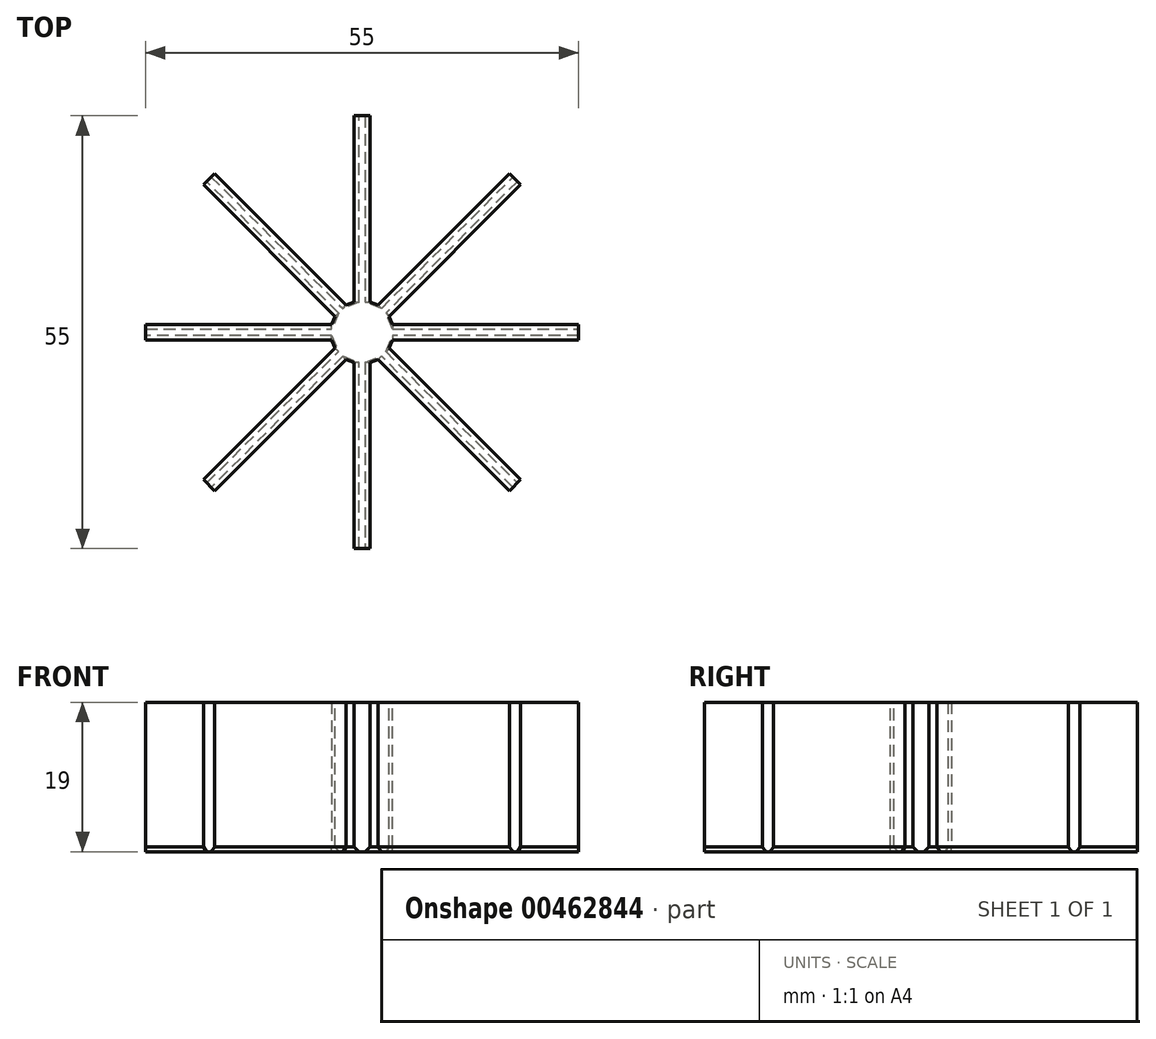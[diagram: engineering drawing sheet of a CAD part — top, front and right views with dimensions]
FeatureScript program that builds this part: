
annotation { "Feature Type Name" : "Feature", "Feature Type Description" : "" }
export const myFeature = defineFeature(function(context is Context, id is Id, definition is map)
    precondition{}
    {
        {
            var Q0;
            Q0=qCreatedBy(makeId("Top.planeOp"),FACE);
            var sketch = newSketch(context, id + "F0", { "sketchPlane" : qUnion([Q0])});
            skLineSegment(sketch, "E0.bottom", {"start": v(0, 0) * mm, "end": v(-2, 0) * mm});
            skLineSegment(sketch, "E0.top", {"start": v(0, 55) * mm, "end": v(-2, 55) * mm});
            skLineSegment(sketch, "E0.left", {"start": v(0, 0) * mm, "end": v(0, 55) * mm});
            skLineSegment(sketch, "E0.right", {"start": v(-2, 0) * mm, "end": v(-2, 55) * mm});
            skLineSegment(sketch, "E1", {"start": v(0, 0) * mm, "end": v(13.96, 0) * mm});
            skLineSegment(sketch, "E2", {"start": v(18.5, 0) * mm, "end": v(26.01, 0) * mm});
            skSolve(sketch);
        }
        {
            var Q0;
            Q0=makeQuery(id+"F0.imprint","IMPRINT",FACE,{"disambiguationData":[TD([[makeQuery(id+"F0.imprint","IMPRINT",EDGE,{"derivedFrom":sQuery(id+"F0.wireOp",EDGE,"E0.bottom")}),-1.0]])]});
            extrude(context, id + "F1", {"entities" : qUnion([Q0]), "depth" : 19 * mm});
        }
        {
            var Q0;
            Q0=qCreatedBy(makeId("Top.planeOp"),FACE);
            var sketch = newSketch(context, id + "F2", { "sketchPlane" : qUnion([Q0])});
            skLineSegment(sketch, "E3", {"start": v(13.67, 0) * mm, "end": v(36.23, 0) * mm});
            skSolve(sketch);
        }
        {
            var Q0;
            Q0=makeQuery(id+"F1.opExtrude","SWEPT_BODY",BODY,{"disambiguationData":[OSD([sQuery(id+"F0.wireOp",EDGE,"E0.bottom"),sQuery(id+"F0.wireOp",EDGE,"E0.top"),sQuery(id+"F0.wireOp",EDGE,"E0.left"),sQuery(id+"F0.wireOp",EDGE,"E0.right")])]});
            var Q1;
            Q1=sQuery(id+"F2.wireOp",EDGE,"E3");
            transform(context, id + "F3", {"entities" : qUnion([Q0]), "transformType" : TransformType.TRANSLATION_DISTANCE, "transformDirection" : qUnion([Q1]), "distance" : 1 * mm, "makeCopy" : false});
        }
        {
            var Q0;
            Q0=qCreatedBy(makeId("Top.planeOp"),FACE);
            var sketch = newSketch(context, id + "F4", { "sketchPlane" : qUnion([Q0])});
            skLineSegment(sketch, "E4", {"start": v(0, 62.06) * mm, "end": v(0, 72.35) * mm});
            skSolve(sketch);
        }
        {
            var Q0;
            Q0=makeQuery(id+"F1.opExtrude","SWEPT_BODY",BODY,{"disambiguationData":[OSD([sQuery(id+"F0.wireOp",EDGE,"E0.bottom"),sQuery(id+"F0.wireOp",EDGE,"E0.top"),sQuery(id+"F0.wireOp",EDGE,"E0.left"),sQuery(id+"F0.wireOp",EDGE,"E0.right")])]});
            var Q1;
            Q1=sQuery(id+"F4.wireOp",EDGE,"E4");
            transform(context, id + "F5", {"entities" : qUnion([Q0]), "transformType" : TransformType.TRANSLATION_DISTANCE, "transformDirection" : qUnion([Q1]), "distance" : 27.5 * mm, "oppositeDirection" : true, "makeCopy" : false});
        }
        {
            var Q0;
            Q0=qCreatedBy(makeId("Front.planeOp"),FACE);
            var sketch = newSketch(context, id + "F6", { "sketchPlane" : qUnion([Q0])});
            skLineSegment(sketch, "E5", {"start": v(0, 0) * mm, "end": v(0, 25.58) * mm});
            skSolve(sketch);
        }
        {
            var Q0;
            Q0=makeQuery(id+"F1.opExtrude","SWEPT_BODY",BODY,{"disambiguationData":[OSD([sQuery(id+"F0.wireOp",EDGE,"E0.bottom"),sQuery(id+"F0.wireOp",EDGE,"E0.top"),sQuery(id+"F0.wireOp",EDGE,"E0.left"),sQuery(id+"F0.wireOp",EDGE,"E0.right")])]});
            var Q1;
            Q1=sQuery(id+"F6.wireOp",EDGE,"E5");
            circularPattern(context, id + "F7", {"entities" : qUnion([Q0]), "axis" : qUnion([Q1]), "angle" : 360 * degree, "instanceCount" : 8, "equalSpace" : true});
        }
        {
            var Q0;
            Q0=makeQuery(id+"F1.opExtrude","SWEPT_BODY",BODY,{"disambiguationData":[OSD([sQuery(id+"F0.wireOp",EDGE,"E0.bottom"),sQuery(id+"F0.wireOp",EDGE,"E0.top"),sQuery(id+"F0.wireOp",EDGE,"E0.left"),sQuery(id+"F0.wireOp",EDGE,"E0.right")])]});
            var Q1;
            Q1=makeQuery(id+"F7.opPattern","COPY",BODY,{"derivedFrom":makeQuery(id+"F1.opExtrude","SWEPT_BODY",BODY,{"disambiguationData":[OSD([sQuery(id+"F0.wireOp",EDGE,"E0.bottom"),sQuery(id+"F0.wireOp",EDGE,"E0.top"),sQuery(id+"F0.wireOp",EDGE,"E0.left"),sQuery(id+"F0.wireOp",EDGE,"E0.right")])]}),"instanceName":"1"});
            var Q2;
            Q2=makeQuery(id+"F7.opPattern","COPY",BODY,{"derivedFrom":makeQuery(id+"F1.opExtrude","SWEPT_BODY",BODY,{"disambiguationData":[OSD([sQuery(id+"F0.wireOp",EDGE,"E0.bottom"),sQuery(id+"F0.wireOp",EDGE,"E0.top"),sQuery(id+"F0.wireOp",EDGE,"E0.left"),sQuery(id+"F0.wireOp",EDGE,"E0.right")])]}),"instanceName":"2"});
            var Q3;
            Q3=makeQuery(id+"F7.opPattern","COPY",BODY,{"derivedFrom":makeQuery(id+"F1.opExtrude","SWEPT_BODY",BODY,{"disambiguationData":[OSD([sQuery(id+"F0.wireOp",EDGE,"E0.bottom"),sQuery(id+"F0.wireOp",EDGE,"E0.top"),sQuery(id+"F0.wireOp",EDGE,"E0.left"),sQuery(id+"F0.wireOp",EDGE,"E0.right")])]}),"instanceName":"3"});
            var Q4;
            Q4=makeQuery(id+"F7.opPattern","COPY",BODY,{"derivedFrom":makeQuery(id+"F1.opExtrude","SWEPT_BODY",BODY,{"disambiguationData":[OSD([sQuery(id+"F0.wireOp",EDGE,"E0.bottom"),sQuery(id+"F0.wireOp",EDGE,"E0.top"),sQuery(id+"F0.wireOp",EDGE,"E0.left"),sQuery(id+"F0.wireOp",EDGE,"E0.right")])]}),"instanceName":"4"});
            var Q5;
            Q5=makeQuery(id+"F7.opPattern","COPY",BODY,{"derivedFrom":makeQuery(id+"F1.opExtrude","SWEPT_BODY",BODY,{"disambiguationData":[OSD([sQuery(id+"F0.wireOp",EDGE,"E0.bottom"),sQuery(id+"F0.wireOp",EDGE,"E0.top"),sQuery(id+"F0.wireOp",EDGE,"E0.left"),sQuery(id+"F0.wireOp",EDGE,"E0.right")])]}),"instanceName":"5"});
            var Q6;
            Q6=makeQuery(id+"F7.opPattern","COPY",BODY,{"derivedFrom":makeQuery(id+"F1.opExtrude","SWEPT_BODY",BODY,{"disambiguationData":[OSD([sQuery(id+"F0.wireOp",EDGE,"E0.bottom"),sQuery(id+"F0.wireOp",EDGE,"E0.top"),sQuery(id+"F0.wireOp",EDGE,"E0.left"),sQuery(id+"F0.wireOp",EDGE,"E0.right")])]}),"instanceName":"6"});
            var Q7;
            Q7=makeQuery(id+"F7.opPattern","COPY",BODY,{"derivedFrom":makeQuery(id+"F1.opExtrude","SWEPT_BODY",BODY,{"disambiguationData":[OSD([sQuery(id+"F0.wireOp",EDGE,"E0.bottom"),sQuery(id+"F0.wireOp",EDGE,"E0.top"),sQuery(id+"F0.wireOp",EDGE,"E0.left"),sQuery(id+"F0.wireOp",EDGE,"E0.right")])]}),"instanceName":"7"});
            booleanBodies(context, id + "F8", {"operationType" : BooleanOperationType.UNION, "tools" : qUnion([Q0, Q1, Q2, Q3, Q4, Q5, Q6, Q7])});
        }
        {
            var Q0;
            {var subQ0=sQuery(id+"F0.wireOp",EDGE,"E0.left");var subQ3=makeQuery(id+"F1.opExtrude","SWEPT_FACE",FACE,{"disambiguationData":[OSD([subQ0])]});Q0=makeQuery(id+"F8.opBoolean","SPLIT",EDGE,{"disambiguationData":[TD([subQ3])],"derivedFrom":makeQuery(id+"F7.opPattern","COPY",EDGE,{"derivedFrom":makeQuery(id+"F1.opExtrude","CAP_EDGE",EDGE,{"disambiguationData":[OSD([subQ0])],"isStart":true}),"instanceName":"3"})});}
            var Q1;
            {var subQ0=sQuery(id+"F0.wireOp",EDGE,"E0.left");var subQ1=sQuery(id+"F0.wireOp",EDGE,"E0.top");Q1=makeQuery(id+"F8.opBoolean","SPLIT",EDGE,{"disambiguationData":[TD([makeQuery(id+"F1.opExtrude","SWEPT_FACE",FACE,{"disambiguationData":[OSD([subQ1])]})])],"derivedFrom":makeQuery(id+"F1.opExtrude","CAP_EDGE",EDGE,{"disambiguationData":[OSD([subQ0])],"isStart":true})});}
            var Q2;
            {var subQ0=sQuery(id+"F0.wireOp",EDGE,"E0.right");var subQ2=sQuery(id+"F0.wireOp",EDGE,"E0.top");Q2=makeQuery(id+"F8.opBoolean","SPLIT",EDGE,{"disambiguationData":[TD([makeQuery(id+"F1.opExtrude","SWEPT_FACE",FACE,{"disambiguationData":[OSD([subQ2])]})])],"derivedFrom":makeQuery(id+"F1.opExtrude","CAP_EDGE",EDGE,{"disambiguationData":[OSD([subQ0])],"isStart":true})});}
            var Q3;
            {var subQ0=sQuery(id+"F0.wireOp",EDGE,"E0.right");var subQ1=sQuery(id+"F0.wireOp",EDGE,"E0.left");Q3=makeQuery(id+"F8.opBoolean","SPLIT",EDGE,{"disambiguationData":[TD([makeQuery(id+"F1.opExtrude","SWEPT_FACE",FACE,{"disambiguationData":[OSD([subQ0])]})])],"derivedFrom":makeQuery(id+"F7.opPattern","COPY",EDGE,{"derivedFrom":makeQuery(id+"F1.opExtrude","CAP_EDGE",EDGE,{"disambiguationData":[OSD([subQ1])],"isStart":true}),"instanceName":"1"})});}
            var Q4;
            {var subQ0=sQuery(id+"F0.wireOp",EDGE,"E0.right");var subQ2=sQuery(id+"F0.wireOp",EDGE,"E0.top");Q4=makeQuery(id+"F8.opBoolean","SPLIT",EDGE,{"disambiguationData":[TD([makeQuery(id+"F7.opPattern","COPY",FACE,{"derivedFrom":makeQuery(id+"F1.opExtrude","SWEPT_FACE",FACE,{"disambiguationData":[OSD([subQ2])]}),"instanceName":"1"})])],"derivedFrom":makeQuery(id+"F7.opPattern","COPY",EDGE,{"derivedFrom":makeQuery(id+"F1.opExtrude","CAP_EDGE",EDGE,{"disambiguationData":[OSD([subQ0])],"isStart":true}),"instanceName":"1"})});}
            var Q5;
            {var subQ0=sQuery(id+"F0.wireOp",EDGE,"E0.right");var subQ2=sQuery(id+"F0.wireOp",EDGE,"E0.top");Q5=makeQuery(id+"F8.opBoolean","SPLIT",EDGE,{"disambiguationData":[TD([makeQuery(id+"F7.opPattern","COPY",FACE,{"derivedFrom":makeQuery(id+"F1.opExtrude","SWEPT_FACE",FACE,{"disambiguationData":[OSD([subQ2])]}),"instanceName":"2"})])],"derivedFrom":makeQuery(id+"F7.opPattern","COPY",EDGE,{"derivedFrom":makeQuery(id+"F1.opExtrude","CAP_EDGE",EDGE,{"disambiguationData":[OSD([subQ0])],"isStart":true}),"instanceName":"2"})});}
            var Q6;
            {var subQ0=sQuery(id+"F0.wireOp",EDGE,"E0.right");var subQ1=sQuery(id+"F0.wireOp",EDGE,"E0.left");Q6=makeQuery(id+"F8.opBoolean","SPLIT",EDGE,{"disambiguationData":[TD([makeQuery(id+"F7.opPattern","COPY",FACE,{"derivedFrom":makeQuery(id+"F1.opExtrude","SWEPT_FACE",FACE,{"disambiguationData":[OSD([subQ0])]}),"instanceName":"2"})])],"derivedFrom":makeQuery(id+"F7.opPattern","COPY",EDGE,{"derivedFrom":makeQuery(id+"F1.opExtrude","CAP_EDGE",EDGE,{"disambiguationData":[OSD([subQ1])],"isStart":true}),"instanceName":"3"})});}
            var Q7;
            {var subQ0=sQuery(id+"F0.wireOp",EDGE,"E0.right");var subQ3=makeQuery(id+"F1.opExtrude","SWEPT_FACE",FACE,{"disambiguationData":[OSD([subQ0])]});Q7=makeQuery(id+"F8.opBoolean","SPLIT",EDGE,{"disambiguationData":[TD([subQ3])],"derivedFrom":makeQuery(id+"F7.opPattern","COPY",EDGE,{"derivedFrom":makeQuery(id+"F1.opExtrude","CAP_EDGE",EDGE,{"disambiguationData":[OSD([subQ0])],"isStart":true}),"instanceName":"3"})});}
            var Q8;
            {var subQ1=sQuery(id+"F0.wireOp",EDGE,"E0.left");var subQ2=sQuery(id+"F0.wireOp",EDGE,"E0.bottom");Q8=makeQuery(id+"F8.opBoolean","SPLIT",EDGE,{"disambiguationData":[TD([makeQuery(id+"F1.opExtrude","SWEPT_FACE",FACE,{"disambiguationData":[OSD([subQ2])]})])],"derivedFrom":makeQuery(id+"F1.opExtrude","CAP_EDGE",EDGE,{"disambiguationData":[OSD([subQ1])],"isStart":true})});}
            var Q9;
            {var subQ0=sQuery(id+"F0.wireOp",EDGE,"E0.right");var subQ1=sQuery(id+"F0.wireOp",EDGE,"E0.left");Q9=makeQuery(id+"F8.opBoolean","SPLIT",EDGE,{"disambiguationData":[TD([makeQuery(id+"F1.opExtrude","SWEPT_FACE",FACE,{"disambiguationData":[OSD([subQ1])]})])],"derivedFrom":makeQuery(id+"F7.opPattern","COPY",EDGE,{"derivedFrom":makeQuery(id+"F1.opExtrude","CAP_EDGE",EDGE,{"disambiguationData":[OSD([subQ0])],"isStart":true}),"instanceName":"1"})});}
            var Q10;
            {var subQ1=sQuery(id+"F0.wireOp",EDGE,"E0.left");var subQ2=sQuery(id+"F0.wireOp",EDGE,"E0.bottom");Q10=makeQuery(id+"F8.opBoolean","SPLIT",EDGE,{"disambiguationData":[TD([makeQuery(id+"F7.opPattern","COPY",FACE,{"derivedFrom":makeQuery(id+"F1.opExtrude","SWEPT_FACE",FACE,{"disambiguationData":[OSD([subQ2])]}),"instanceName":"1"})])],"derivedFrom":makeQuery(id+"F7.opPattern","COPY",EDGE,{"derivedFrom":makeQuery(id+"F1.opExtrude","CAP_EDGE",EDGE,{"disambiguationData":[OSD([subQ1])],"isStart":true}),"instanceName":"1"})});}
            var Q11;
            {var subQ0=sQuery(id+"F0.wireOp",EDGE,"E0.right");var subQ1=sQuery(id+"F0.wireOp",EDGE,"E0.left");Q11=makeQuery(id+"F8.opBoolean","SPLIT",EDGE,{"disambiguationData":[TD([makeQuery(id+"F7.opPattern","COPY",FACE,{"derivedFrom":makeQuery(id+"F1.opExtrude","SWEPT_FACE",FACE,{"disambiguationData":[OSD([subQ1])]}),"instanceName":"1"})])],"derivedFrom":makeQuery(id+"F7.opPattern","COPY",EDGE,{"derivedFrom":makeQuery(id+"F1.opExtrude","CAP_EDGE",EDGE,{"disambiguationData":[OSD([subQ0])],"isStart":true}),"instanceName":"2"})});}
            var Q12;
            {var subQ1=sQuery(id+"F0.wireOp",EDGE,"E0.left");var subQ2=sQuery(id+"F0.wireOp",EDGE,"E0.bottom");Q12=makeQuery(id+"F8.opBoolean","SPLIT",EDGE,{"disambiguationData":[TD([makeQuery(id+"F7.opPattern","COPY",FACE,{"derivedFrom":makeQuery(id+"F1.opExtrude","SWEPT_FACE",FACE,{"disambiguationData":[OSD([subQ2])]}),"instanceName":"2"})])],"derivedFrom":makeQuery(id+"F7.opPattern","COPY",EDGE,{"derivedFrom":makeQuery(id+"F1.opExtrude","CAP_EDGE",EDGE,{"disambiguationData":[OSD([subQ1])],"isStart":true}),"instanceName":"2"})});}
            var Q13;
            {var subQ0=sQuery(id+"F0.wireOp",EDGE,"E0.right");var subQ1=sQuery(id+"F0.wireOp",EDGE,"E0.left");Q13=makeQuery(id+"F8.opBoolean","SPLIT",EDGE,{"disambiguationData":[TD([makeQuery(id+"F7.opPattern","COPY",FACE,{"derivedFrom":makeQuery(id+"F1.opExtrude","SWEPT_FACE",FACE,{"disambiguationData":[OSD([subQ1])]}),"instanceName":"2"})])],"derivedFrom":makeQuery(id+"F7.opPattern","COPY",EDGE,{"derivedFrom":makeQuery(id+"F1.opExtrude","CAP_EDGE",EDGE,{"disambiguationData":[OSD([subQ0])],"isStart":true}),"instanceName":"3"})});}
            var Q14;
            {var subQ0=makeQuery(id+"F1.opExtrude","SWEPT_FACE",FACE,{"disambiguationData":[OSD([sQuery(id+"F0.wireOp",EDGE,"E0.right")])]});var subQ1=makeQuery(id+"F1.opExtrude","SWEPT_FACE",FACE,{"disambiguationData":[OSD([sQuery(id+"F0.wireOp",EDGE,"E0.left")])]});Q14=makeQuery(id+"F8.opBoolean","INTERSECT",EDGE,{"derivedFrom":[subQ1,makeQuery(id+"F7.opPattern","COPY",FACE,{"derivedFrom":subQ1,"instanceName":"3"}),makeQuery(id+"F7.opPattern","COPY",FACE,{"derivedFrom":subQ0,"instanceName":"4"}),makeQuery(id+"F7.opPattern","COPY",FACE,{"derivedFrom":subQ0,"instanceName":"7"})]});}
            var Q15;
            {var subQ0=makeQuery(id+"F1.opExtrude","SWEPT_FACE",FACE,{"disambiguationData":[OSD([sQuery(id+"F0.wireOp",EDGE,"E0.left")])]});var subQ1=makeQuery(id+"F1.opExtrude","SWEPT_FACE",FACE,{"disambiguationData":[OSD([sQuery(id+"F0.wireOp",EDGE,"E0.right")])]});Q15=makeQuery(id+"F8.opBoolean","INTERSECT",EDGE,{"derivedFrom":[makeQuery(id+"F7.opPattern","COPY",FACE,{"derivedFrom":subQ0,"instanceName":"2"}),makeQuery(id+"F7.opPattern","COPY",FACE,{"derivedFrom":subQ1,"instanceName":"3"}),makeQuery(id+"F7.opPattern","COPY",FACE,{"derivedFrom":subQ1,"instanceName":"6"}),makeQuery(id+"F7.opPattern","COPY",FACE,{"derivedFrom":subQ0,"instanceName":"7"})]});}
            var Q16;
            {var subQ0=makeQuery(id+"F1.opExtrude","SWEPT_FACE",FACE,{"disambiguationData":[OSD([sQuery(id+"F0.wireOp",EDGE,"E0.left")])]});var subQ1=makeQuery(id+"F1.opExtrude","SWEPT_FACE",FACE,{"disambiguationData":[OSD([sQuery(id+"F0.wireOp",EDGE,"E0.right")])]});Q16=makeQuery(id+"F8.opBoolean","INTERSECT",EDGE,{"derivedFrom":[makeQuery(id+"F7.opPattern","COPY",FACE,{"derivedFrom":subQ0,"instanceName":"1"}),makeQuery(id+"F7.opPattern","COPY",FACE,{"derivedFrom":subQ1,"instanceName":"2"}),makeQuery(id+"F7.opPattern","COPY",FACE,{"derivedFrom":subQ1,"instanceName":"5"}),makeQuery(id+"F7.opPattern","COPY",FACE,{"derivedFrom":subQ0,"instanceName":"6"})]});}
            var Q17;
            {var subQ0=makeQuery(id+"F1.opExtrude","SWEPT_FACE",FACE,{"disambiguationData":[OSD([sQuery(id+"F0.wireOp",EDGE,"E0.left")])]});var subQ1=makeQuery(id+"F1.opExtrude","SWEPT_FACE",FACE,{"disambiguationData":[OSD([sQuery(id+"F0.wireOp",EDGE,"E0.right")])]});Q17=makeQuery(id+"F8.opBoolean","INTERSECT",EDGE,{"derivedFrom":[subQ0,makeQuery(id+"F7.opPattern","COPY",FACE,{"derivedFrom":subQ1,"instanceName":"1"}),makeQuery(id+"F7.opPattern","COPY",FACE,{"derivedFrom":subQ1,"instanceName":"4"}),makeQuery(id+"F7.opPattern","COPY",FACE,{"derivedFrom":subQ0,"instanceName":"5"})]});}
            var Q18;
            {var subQ0=makeQuery(id+"F1.opExtrude","SWEPT_FACE",FACE,{"disambiguationData":[OSD([sQuery(id+"F0.wireOp",EDGE,"E0.right")])]});var subQ1=makeQuery(id+"F1.opExtrude","SWEPT_FACE",FACE,{"disambiguationData":[OSD([sQuery(id+"F0.wireOp",EDGE,"E0.left")])]});Q18=makeQuery(id+"F8.opBoolean","INTERSECT",EDGE,{"derivedFrom":[makeQuery(id+"F7.opPattern","COPY",FACE,{"derivedFrom":subQ0,"instanceName":"2"}),makeQuery(id+"F7.opPattern","COPY",FACE,{"derivedFrom":subQ1,"instanceName":"3"}),makeQuery(id+"F7.opPattern","COPY",FACE,{"derivedFrom":subQ1,"instanceName":"6"}),makeQuery(id+"F7.opPattern","COPY",FACE,{"derivedFrom":subQ0,"instanceName":"7"})]});}
            var Q19;
            {var subQ0=makeQuery(id+"F1.opExtrude","SWEPT_FACE",FACE,{"disambiguationData":[OSD([sQuery(id+"F0.wireOp",EDGE,"E0.right")])]});var subQ1=makeQuery(id+"F1.opExtrude","SWEPT_FACE",FACE,{"disambiguationData":[OSD([sQuery(id+"F0.wireOp",EDGE,"E0.left")])]});Q19=makeQuery(id+"F8.opBoolean","INTERSECT",EDGE,{"derivedFrom":[makeQuery(id+"F7.opPattern","COPY",FACE,{"derivedFrom":subQ0,"instanceName":"1"}),makeQuery(id+"F7.opPattern","COPY",FACE,{"derivedFrom":subQ1,"instanceName":"2"}),makeQuery(id+"F7.opPattern","COPY",FACE,{"derivedFrom":subQ1,"instanceName":"5"}),makeQuery(id+"F7.opPattern","COPY",FACE,{"derivedFrom":subQ0,"instanceName":"6"})]});}
            var Q20;
            {var subQ0=makeQuery(id+"F1.opExtrude","SWEPT_FACE",FACE,{"disambiguationData":[OSD([sQuery(id+"F0.wireOp",EDGE,"E0.right")])]});var subQ1=makeQuery(id+"F1.opExtrude","SWEPT_FACE",FACE,{"disambiguationData":[OSD([sQuery(id+"F0.wireOp",EDGE,"E0.left")])]});Q20=makeQuery(id+"F8.opBoolean","INTERSECT",EDGE,{"derivedFrom":[subQ0,makeQuery(id+"F7.opPattern","COPY",FACE,{"derivedFrom":subQ1,"instanceName":"1"}),makeQuery(id+"F7.opPattern","COPY",FACE,{"derivedFrom":subQ1,"instanceName":"4"}),makeQuery(id+"F7.opPattern","COPY",FACE,{"derivedFrom":subQ0,"instanceName":"5"})]});}
            var Q21;
            {var subQ0=makeQuery(id+"F1.opExtrude","SWEPT_FACE",FACE,{"disambiguationData":[OSD([sQuery(id+"F0.wireOp",EDGE,"E0.left")])]});var subQ1=makeQuery(id+"F1.opExtrude","SWEPT_FACE",FACE,{"disambiguationData":[OSD([sQuery(id+"F0.wireOp",EDGE,"E0.right")])]});Q21=makeQuery(id+"F8.opBoolean","INTERSECT",EDGE,{"derivedFrom":[subQ1,makeQuery(id+"F7.opPattern","COPY",FACE,{"derivedFrom":subQ1,"instanceName":"3"}),makeQuery(id+"F7.opPattern","COPY",FACE,{"derivedFrom":subQ0,"instanceName":"4"}),makeQuery(id+"F7.opPattern","COPY",FACE,{"derivedFrom":subQ0,"instanceName":"7"})]});}
            chamfer(context, id + "F9", {"entities" : qUnion([Q0, Q1, Q2, Q3, Q4, Q5, Q6, Q7, Q8, Q9, Q10, Q11, Q12, Q13, Q14, Q15, Q16, Q17, Q18, Q19, Q20, Q21]), "width" : 0.6 * mm, "tangentPropagation" : true});
        }
    });
